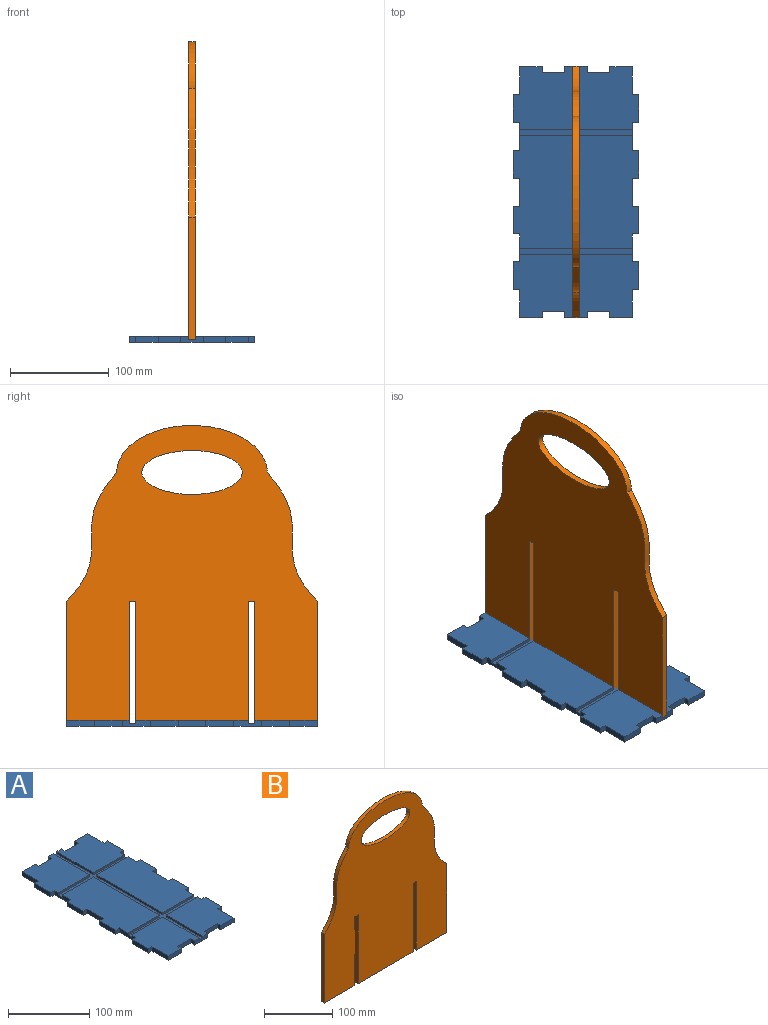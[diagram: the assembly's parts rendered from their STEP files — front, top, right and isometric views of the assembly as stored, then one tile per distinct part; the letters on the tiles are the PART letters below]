
ASSEMBLY  parts=2 mates=1
PART A: 74 faces, bbox 127x254x6.4 mm
  f0: plane 63.5x60.33mm, normal (0,0,1), area 3461.5mm2, adj f3,f8,f12,f27,f28,f29,f30,f31
  f1: plane 114.3x60.33mm, normal (0,0,1), area 6527.8mm2, adj f2,f3,f9,f20,f21,f22,f23,f24
  f2: plane 28.22x6.35mm, normal (1,0,0), area 159mm2, adj f1,f14,f19,f20,f62,f63,f70,f71
  f3: plane 28.22x6.35mm, normal (1,0,0), area 159mm2, adj f0,f1,f26,f27,f62,f63,f72,f73
  f4: plane 28.22x6.35mm, normal (-1,0,0), area 159mm2, adj f6,f7,f42,f43,f62,f63,f68,f69
  f5: plane 28.22x6.35mm, normal (-1,0,0), area 159mm2, adj f7,f49,f50,f61,f62,f63,f66,f67
  f6: plane 63.5x60.33mm, normal (0,0,1), area 3461.5mm2, adj f4,f10,f12,f35,f36,f37,f38,f39
  f7: plane 114.3x60.33mm, normal (0,0,1), area 6527.8mm2, adj f4,f5,f11,f43,f44,f45,f46,f47
  f8: plane 63.5x3.18mm, normal (-1,0,0), area 201.6mm2, adj f0,f12,f63,f72
  f9: plane 114.3x3.18mm, normal (-1,0,0), area 362.9mm2, adj f1,f63,f70,f73
  f10: plane 63.5x3.18mm, normal (1,0,0), area 201.6mm2, adj f6,f12,f63,f68
  f11: plane 114.3x3.18mm, normal (1,0,0), area 362.9mm2, adj f7,f63,f66,f69
  f12: plane 22.86x6.35mm, normal (0,1,0), area 125mm2, adj f0,f6,f8,f10,f34,f35,f62,f63
  f13: plane 22.86x6.35mm, normal (0,-1,0), area 125mm2, adj f14,f57,f58,f61,f62,f63,f64,f65
  f14: plane 63.5x60.33mm, normal (0,0,1), area 3461.5mm2, adj f2,f13,f15,f16,f17,f18,f19,f58
  f15: plane 22.86x6.35mm, normal (0,-1,0), area 145.2mm2, adj f14,f16,f60,f62
  f16: plane 28.22x6.35mm, normal (1,0,0), area 179.2mm2, adj f14,f15,f17,f62
  f17: plane 6.35x6.35mm, normal (0,-1,0), area 40.3mm2, adj f14,f16,f18,f62
  f18: plane 28.22x6.35mm, normal (1,0,0), area 179.2mm2, adj f14,f17,f19,f62
  f19: plane 6.35x6.35mm, normal (0,1,0), area 40.3mm2, adj f2,f14,f18,f62
  f20: plane 6.35x6.35mm, normal (0,-1,0), area 40.3mm2, adj f1,f2,f21,f62
  f21: plane 28.22x6.35mm, normal (1,0,0), area 179.2mm2, adj f1,f20,f22,f62
  f22: plane 6.35x6.35mm, normal (0,1,0), area 40.3mm2, adj f1,f21,f23,f62
  f23: plane 28.22x6.35mm, normal (1,0,0), area 179.2mm2, adj f1,f22,f24,f62
  f24: plane 6.35x6.35mm, normal (0,-1,0), area 40.3mm2, adj f1,f23,f25,f62
  f25: plane 28.22x6.35mm, normal (1,0,0), area 179.2mm2, adj f1,f24,f26,f62
  f26: plane 6.35x6.35mm, normal (0,1,0), area 40.3mm2, adj f1,f3,f25,f62
  f27: plane 6.35x6.35mm, normal (0,-1,0), area 40.3mm2, adj f0,f3,f28,f62
  f28: plane 28.22x6.35mm, normal (1,0,0), area 179.2mm2, adj f0,f27,f29,f62
  f29: plane 6.35x6.35mm, normal (0,1,0), area 40.3mm2, adj f0,f28,f30,f62
  f30: plane 28.22x6.35mm, normal (1,0,0), area 179.2mm2, adj f0,f29,f31,f62
  f31: plane 22.86x6.35mm, normal (0,1,0), area 145.2mm2, adj f0,f30,f32,f62
  f32: plane 6.35x6.35mm, normal (-1,0,0), area 40.3mm2, adj f0,f31,f33,f62
  f33: plane 22.86x6.35mm, normal (0,1,0), area 145.2mm2, adj f0,f32,f34,f62
  f34: plane 6.35x6.35mm, normal (1,0,0), area 40.3mm2, adj f0,f12,f33,f62
  f35: plane 6.35x6.35mm, normal (-1,0,0), area 40.3mm2, adj f6,f12,f36,f62
  f36: plane 22.86x6.35mm, normal (0,1,0), area 145.2mm2, adj f6,f35,f37,f62
  f37: plane 6.35x6.35mm, normal (1,0,0), area 40.3mm2, adj f6,f36,f38,f62
  f38: plane 22.86x6.35mm, normal (0,1,0), area 145.2mm2, adj f6,f37,f39,f62
  f39: plane 28.22x6.35mm, normal (-1,0,0), area 179.2mm2, adj f6,f38,f40,f62
  f40: plane 6.35x6.35mm, normal (0,1,0), area 40.3mm2, adj f6,f39,f41,f62
  f41: plane 28.22x6.35mm, normal (-1,0,0), area 179.2mm2, adj f6,f40,f42,f62
  f42: plane 6.35x6.35mm, normal (0,-1,0), area 40.3mm2, adj f4,f6,f41,f62
  f43: plane 6.35x6.35mm, normal (0,1,0), area 40.3mm2, adj f4,f7,f44,f62
  f44: plane 28.22x6.35mm, normal (-1,0,0), area 179.2mm2, adj f7,f43,f45,f62
  f45: plane 6.35x6.35mm, normal (0,-1,0), area 40.3mm2, adj f7,f44,f46,f62
  f46: plane 28.22x6.35mm, normal (-1,0,0), area 179.2mm2, adj f7,f45,f47,f62
  f47: plane 6.35x6.35mm, normal (0,1,0), area 40.3mm2, adj f7,f46,f48,f62
  f48: plane 28.22x6.35mm, normal (-1,0,0), area 179.2mm2, adj f7,f47,f49,f62
  f49: plane 6.35x6.35mm, normal (0,-1,0), area 40.3mm2, adj f5,f7,f48,f62
  f50: plane 6.35x6.35mm, normal (0,1,0), area 40.3mm2, adj f5,f51,f61,f62
  f51: plane 28.22x6.35mm, normal (-1,0,0), area 179.2mm2, adj f50,f52,f61,f62
  f52: plane 6.35x6.35mm, normal (0,-1,0), area 40.3mm2, adj f51,f53,f61,f62
  f53: plane 28.22x6.35mm, normal (-1,0,0), area 179.2mm2, adj f52,f54,f61,f62
  f54: plane 22.86x6.35mm, normal (0,-1,0), area 145.2mm2, adj f53,f55,f61,f62
  f55: plane 6.35x6.35mm, normal (1,0,0), area 40.3mm2, adj f54,f56,f61,f62
  f56: plane 22.86x6.35mm, normal (0,-1,0), area 145.2mm2, adj f55,f57,f61,f62
  f57: plane 6.35x6.35mm, normal (-1,0,0), area 40.3mm2, adj f13,f56,f61,f62
  f58: plane 6.35x6.35mm, normal (1,0,0), area 40.3mm2, adj f13,f14,f59,f62
  f59: plane 22.86x6.35mm, normal (0,-1,0), area 145.2mm2, adj f14,f58,f60,f62
  f60: plane 6.35x6.35mm, normal (-1,0,0), area 40.3mm2, adj f14,f15,f59,f62
  f61: plane 63.5x60.33mm, normal (0,0,1), area 3461.5mm2, adj f5,f13,f50,f51,f52,f53,f54,f55
  f62: plane 254x127mm, normal (0,0,-1), area 29885.2mm2, adj f2,f3,f4,f5,f12,f13,f15,f16
  f63: plane 254x114.3mm, normal (0,0,1), area 2983.9mm2, adj f2,f3,f4,f5,f8,f9,f10,f11
  f64: plane 63.5x3.18mm, normal (-1,0,0), area 201.6mm2, adj f13,f14,f63,f71
  f65: plane 63.5x3.18mm, normal (1,0,0), area 201.6mm2, adj f13,f61,f63,f67
  f66: plane 53.98x3.18mm, normal (0,-1,0), area 171.4mm2, adj f5,f7,f11,f63
  f67: plane 53.98x3.18mm, normal (0,1,0), area 171.4mm2, adj f5,f61,f63,f65
  f68: plane 53.98x3.18mm, normal (0,-1,0), area 171.4mm2, adj f4,f6,f10,f63
  f69: plane 53.98x3.18mm, normal (0,1,0), area 171.4mm2, adj f4,f7,f11,f63
  f70: plane 53.98x3.18mm, normal (0,-1,0), area 171.4mm2, adj f1,f2,f9,f63
  f71: plane 53.98x3.18mm, normal (0,1,0), area 171.4mm2, adj f2,f14,f63,f64
  f72: plane 53.98x3.18mm, normal (0,-1,0), area 171.4mm2, adj f0,f3,f8,f63
  f73: plane 53.98x3.18mm, normal (0,1,0), area 171.4mm2, adj f1,f3,f9,f63
PART B: 17 faces, bbox 254x6.4x301.6 mm
  f0: plane 63.5x6.35mm, normal (0,0,-1), area 403.2mm2, adj f1,f14,f15,f16
  f1: plane 123.83x6.35mm, normal (1,0,0), area 786.3mm2, adj f0,f2,f15,f16
  f2: plane 6.35x6.35mm, normal (0,0,-1), area 40.3mm2, adj f1,f3,f15,f16
  f3: plane 123.83x6.35mm, normal (-1,0,0), area 786.3mm2, adj f2,f4,f15,f16
  f4: plane 114.3x6.35mm, normal (0,0,-1), area 725.8mm2, adj f3,f5,f15,f16
  f5: plane 123.83x6.35mm, normal (1,0,0), area 786.3mm2, adj f4,f6,f15,f16
  f6: plane 6.35x6.35mm, normal (0,0,-1), area 40.3mm2, adj f5,f7,f15,f16
  f7: plane 123.83x6.35mm, normal (-1,0,0), area 786.3mm2, adj f6,f8,f15,f16
  f8: plane 63.5x6.35mm, normal (0,0,-1), area 403.2mm2, adj f7,f9,f15,f16
  f9: plane 123.83x6.35mm, normal (1,0,0), area 786.3mm2, adj f8,f10,f15,f16
  f10: extruded ~130.18x50.8mm, area 918.2mm2, adj f9,f11,f15,f16
  f11: extruded ~152.4x47.63mm, area 1251.6mm2, adj f10,f12,f15,f16
  f12: extruded ~130.18x50.8mm, area 918.2mm2, adj f11,f14,f15,f16
  f13: extruded ~101.6x44.45mm, area 1513.2mm2, adj f15,f16
  f14: plane 123.83x6.35mm, normal (-1,0,0), area 786.3mm2, adj f0,f12,f15,f16
  f15: plane 301.63x254mm, normal (0,-1,0), area 58410.1mm2, adj f0,f1,f2,f3,f4,f5,f6,f7
  f16: plane 301.63x254mm, normal (0,1,0), area 58410.1mm2, adj f0,f1,f2,f3,f4,f5,f6,f7
PLACE A t=(63.5,127,0)mm
PLACE B rot(axis=(0,0,1),90deg) t=(-3.18,-127,3.18)mm
MATE fastened A.f63 <-> B.f4  axis (0,0,1) through (0,0,3.18)mm
